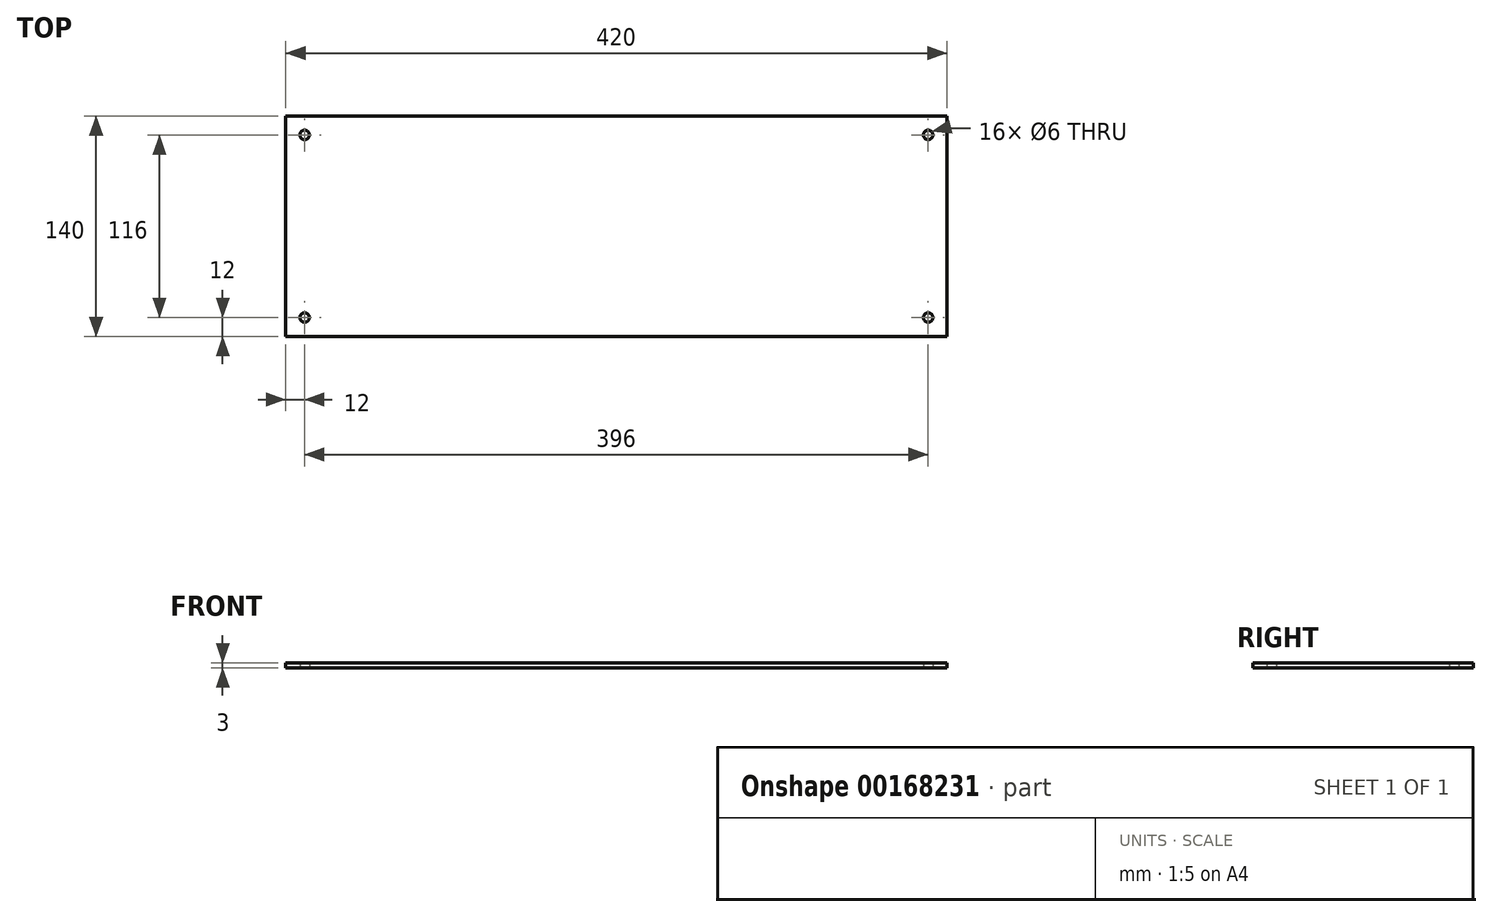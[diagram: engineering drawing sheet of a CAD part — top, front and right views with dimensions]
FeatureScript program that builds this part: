
annotation { "Feature Type Name" : "Feature", "Feature Type Description" : "" }
export const myFeature = defineFeature(function(context is Context, id is Id, definition is map)
    precondition{}
    {
        {
            var Q0;
            Q0=qCreatedBy(makeId("Top.planeOp"),FACE);
            var sketch = newSketch(context, id + "F0", { "sketchPlane" : qUnion([Q0])});
            skLineSegment(sketch, "E0.bottom", {"start": v(210, -70) * mm, "end": v(-210, -70) * mm});
            skLineSegment(sketch, "E0.top", {"start": v(210, 70) * mm, "end": v(-210, 70) * mm});
            skLineSegment(sketch, "E0.left", {"start": v(210, -70) * mm, "end": v(210, 70) * mm});
            skLineSegment(sketch, "E0.right", {"start": v(-210, -70) * mm, "end": v(-210, 70) * mm});
            skPoint(sketch, "E0.middle", {"position": v(0, 0) * mm});
            skLineSegment(sketch, "E1.0", {"start": v(198, 58) * mm, "end": v(-198, 58) * mm, "construction": true});
            skLineSegment(sketch, "E1.1", {"start": v(198, -58) * mm, "end": v(198, 58) * mm, "construction": true});
            skLineSegment(sketch, "E1.2", {"start": v(198, -58) * mm, "end": v(-198, -58) * mm, "construction": true});
            skLineSegment(sketch, "E1.3", {"start": v(-198, -58) * mm, "end": v(-198, 58) * mm, "construction": true});
            skCircle(sketch, "E2", {"center": v(-198, 58) * mm, "radius": 3 * mm});
            skCircle(sketch, "E3", {"center": v(-198, -58) * mm, "radius": 3 * mm});
            skCircle(sketch, "E4", {"center": v(198, 58) * mm, "radius": 3 * mm});
            skCircle(sketch, "E5", {"center": v(198, -58) * mm, "radius": 3 * mm});
            skSolve(sketch);
        }
        {
            var Q0;
            Q0=qSketchRegion(id+"F0",true);
            extrude(context, id + "F1", {"entities" : qUnion([Q0]), "depth" : 3 * mm});
        }
    });
